# Revit family: IS_Intellimix_A7488_BIM_NL
name_source: partatom
category: Plumbing Fixtures
units: mm (PartAtom-declared; Revit-internal decimal feet)

## family parameters
Always vertical = No
Cut with Voids When Loaded = No
OmniClass Number = 23.31.11.00
Part Type = Normal
Room Calculation Point = No
Round Connector Dimension = Use Diameter
Shared = No
Work Plane-Based = No

## types (1)
- A7488AA - INTELLIMIX PREMIUM REMOTE CONTROLLED BASIN FAUCET NO MIXER
    Accessories = https://www.idealstandard.nl
    AreaMeasurement = Internal
    AreaUnits = Millimetres
    BIMObjectName = IS_IdealStandard_Washbasintaps_Intellimix_A7488
    BIMobject category = Taps & Mixers
    BIMobject category code = sanitary-taps-mixers
    BIMobject main category = Sanitary
    BIMobject main category code = sanitary
    BarCode = 4015413349673
    Brand = Ideal Standard
    Brand url = https://www.idealstandard.nl
    Color = Chrome
    ConnectionType = Plumbing
    CurrencyUnit = €
    CurrentRevision = 1
    Date of publishing = 01/04/2021
    Description = Intellimix contactless washbasin faucet with integrated soap dispenser (in foam form). Built-in electronic systems and Bluetooth function.
    DurationUnit = Years
    Edition number = 1
    ExpectedLife = 5
    FaucetFunction = Remote controlled basin faucet
    FaucetOperation = Contactles faucet
    FaucetTopDescription = Contactles faucet
    FaucetType = Remote controlled, contactless basin faucet
    Features = Contactless washbasin faucet with integrated soap dispenser (in foam form). Built-in electronic systems and Bluetooth function.
    Finish = Chrome
    GTIN code = https://4015413349673
    Help = https://www.idealstandard.nl
    IFC Classification = Sanitary Terminal
    IfcExportAs = IfcValveType
    IfcExportType = FAUCET
    Installation instructions = https://www.idealstandard.nl
    InstallationInstructions = https://www.idealstandard.nl
    IsBuiltIn = No
    IsHighPressure = No
    LinearUnits = Millimetres
    MainColor = Chrome
    MaintenanceInformation = https://www.idealstandard.nl
    Manufacturer = Ideal Standard Nederland BV
    Manufacturer name = Ideal Standard
    ManufacturerURL = https://www.idealstandard.nl
    Material = Brass
    Material main = Brass
    MaterialThickness = 0 mm  [stored 0 ft]
    Model = A7488AA
    ModelNumber = A7488AA
    ModelReference = INTELLIMIX PREMIUM REMOTE CONTROLLED BASIN FAUCET NO MIXER
    NBS Reference Code = 45-35-70/371
    NBS Reference Description = Water supply fittings for wash basins and troughs
    Name = Washbasintaps_Intellimix_A7488_IdealStandard
    NettWeight = 3.25
    NominalDepth = 625 mm
    NominalHeight = 151 mm
    NominalLength = 156 mm
    NominalWidth = 52 mm  [stored 0.170604 ft]
    OmniClass Code = 23-31 11 00
    OmniClass Description = Faucets
    Product Guid = 8745909d-70fa-48c3-b8da-0bbf38ad64ab
    Product SKU = A7488
    Product certification = https://www.idealstandard.nl
    Product data url = https://www.idealstandard.nl
    Product family = Sanitary
    Product group = Washbasins
    Product name = Intellimix contactless washbasin faucet with integrated soap dispenser
    Product url = https://www.idealstandard.nl
    ProductInformation = https://www.idealstandard.nl
    QR code = http://bimobject.com
    Shape = Cylindrical
    Size = 151 x 156 x 52 mm
    Space = Internal
    SpareParts = https://www.idealstandard.nl
    Technical description = https://www.idealstandard.nl
    TestPressure = 10 bar
    UNSPSC Code = 301815
    URL = https://www.idealstandard.nl
    Uniclass 1.4 Code = L725111
    Uniclass 1.4 Description = Mixer taps
    Uniclass 2.0 Code = PR-35-79-95
    Uniclass 2.0 Description = Wash Basin And Trough Water Supply Fittings
    Uniclass 2015 Code = Pr_40_20_87_98
    Uniclass 2015 Name = Washbasin taps
    Uniclass2015Code = Pr_40_20_87_98
    Uniclass2015Title = Washbasin taps
    Uniclass2015Version = v1.20
    Version = 1
    VolumeUnits = Litres
    WRASURL = https://www.wrasapprovals.co.uk
    WarrantyDescription = Manufacturer Warranty
    WarrantyDurationUnit = Years
    WorkingPressure = 3 bar
    Youtube clip = https://www.youtube.com

note: [stored X ft] marks values corroborated as IEEE doubles in the binary element streams (Revit-internal decimal feet)

## geometry (parser evidence)
native form markers: Sweep x3
no freeform markers — native parametric forms only
